# Revit family: TD92_SAF048_GRA007_RVT20_R00
name_source: partatom
category: Mobiliário
units: mm (PartAtom-declared; Revit-internal decimal feet)

## family parameters
Com base no plano de trabalho = Não
Compartilhado = Não
Corte com vazios quando carregada = Não
Número OmniClass = 23.40.20.00
Ponto de cálculo do ambiente = Não
Sempre na vertical = Sim
Título OmniClass = General Furniture and Specialties

## types (1)
- TD92_SAF048_GRA007_RVT20_R00
    Descrição = A Cadeira Tramontina Safira em Polipropileno e Fibra de Vidro da linha Summa veio para transformar a sua decoração com seu design inovador. Projetada com uma forma robusta, bonita e moderna, ela é ideal para a sua casa ou escritório, tornando os espaços ainda mais surpreendentes e dando aquele toque de sofisticação que faltava. Além disso, está disponível em diversas cores para você inovar com facilidade.
    Elevação padrão = 0  [stored 0 ft]
    Fabricante = Tramontina Delta S/A
    Modelo = Cadeira Tramontina Safira em Polipropileno e Fibra de Vidro Grafite
    Nota-chave = 92048007
    URL = https://www.tramontinastore.com

note: [stored X ft] marks values corroborated as IEEE doubles in the binary element streams (Revit-internal decimal feet)
